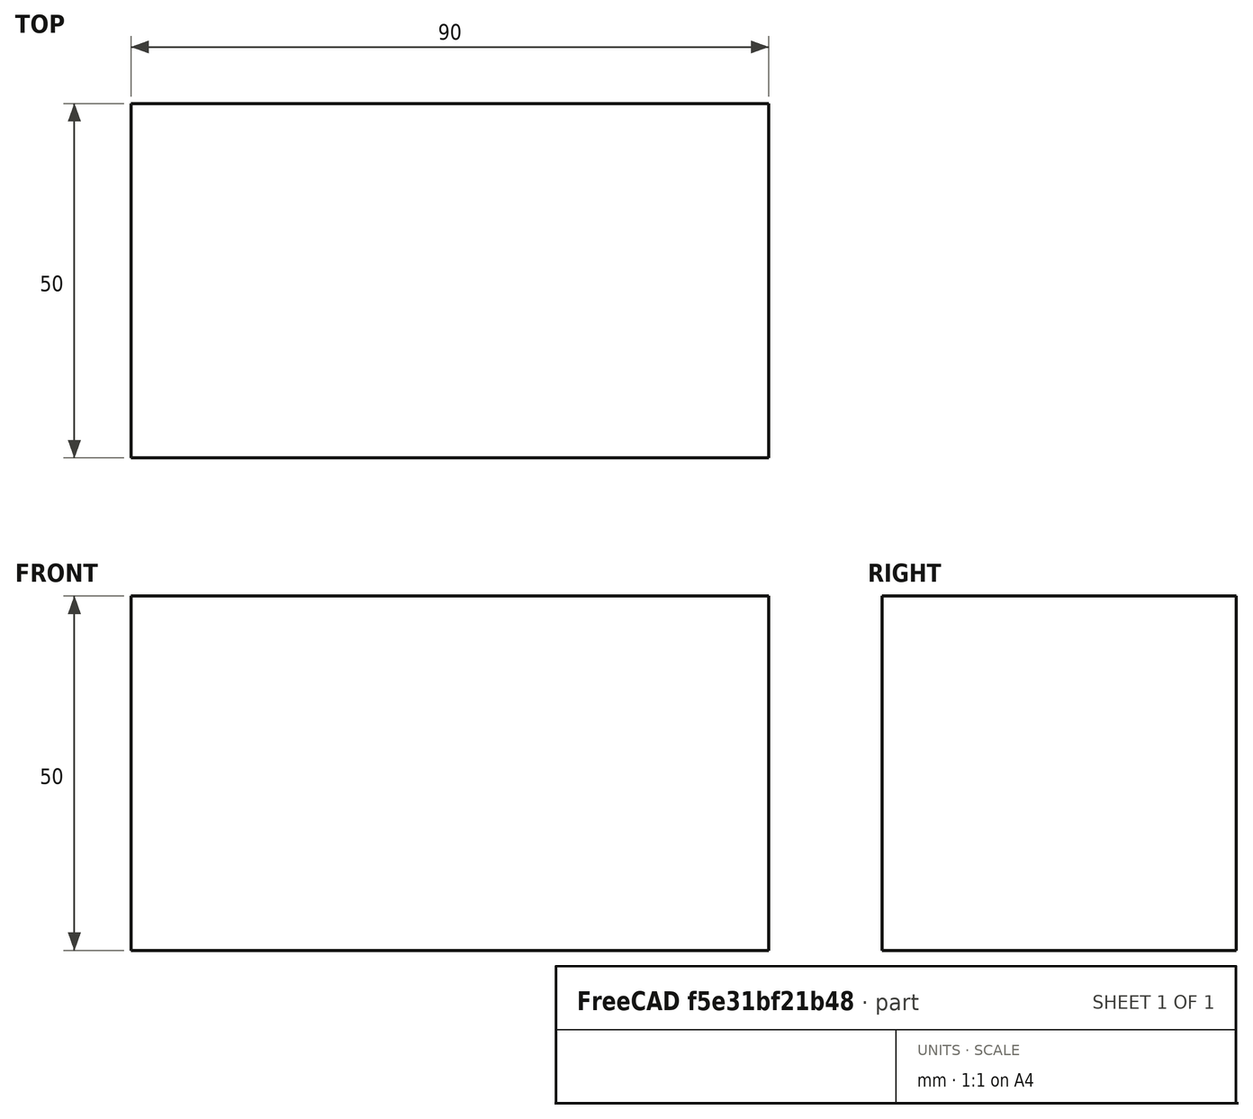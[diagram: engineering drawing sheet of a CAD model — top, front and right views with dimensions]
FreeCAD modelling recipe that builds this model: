
FCSTD DOCUMENT  (FreeCAD 0.15R4671 (Git))
Label: Flat Bar 90x50 EN10058 S235JR
License: All rights reserved
LicenseURL: http://en.wikipedia.org/wiki/All_rights_reserved
objects: Sketcher::SketchObject×1, Part::Extrusion×1
note: 2 computed .brp shape members not serialized (recipe doc carries the construction recipe); baked Part::Feature solids carry a one-line shape summary decoded from their .brp

FEATURE [Sketcher::SketchObject] Sketch
  sketch-geometry (4):
    g0: LineSegment StartX=-45 StartY=-25 StartZ=0 EndX=45 EndY=-25 EndZ=0
    g1: LineSegment StartX=45 StartY=-25 StartZ=0 EndX=45 EndY=25 EndZ=0
    g2: LineSegment StartX=45 StartY=25 StartZ=0 EndX=-45 EndY=25 EndZ=0
    g3: LineSegment StartX=-45 StartY=25 StartZ=0 EndX=-45 EndY=-25 EndZ=0
  constraints (12):
    c: Coincident(g0,g1)
    c: Coincident(g1,g2)
    c: Coincident(g2,g3)
    c: Coincident(g3,g0)
    c: Horizontal(g0)
    c: Horizontal(g2)
    c: Vertical(g1)
    c: Vertical(g3)
    c: Symmetric(g1,g2,g-2)
    c: Symmetric(g0,g1,g-1)
    c: DistanceY(g1) = 50
    c: DistanceX(g0) = 90
FEATURE [Part::Extrusion] Extrude  label="Flat Bar 90x50 EN10058 S235JR"
  Base = -> Sketch
  Dir = (0,0,50)
  Solid = true
